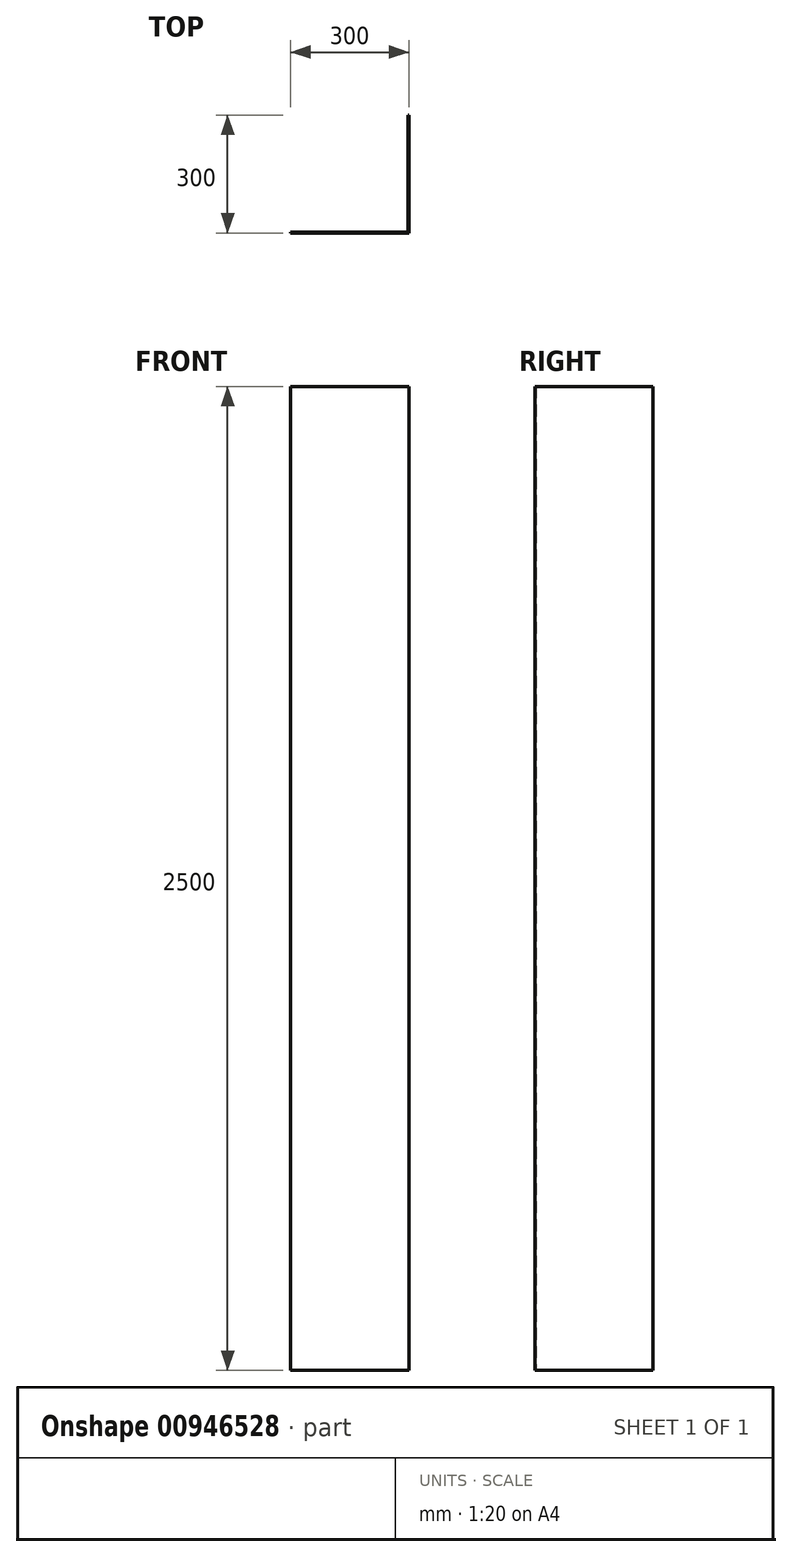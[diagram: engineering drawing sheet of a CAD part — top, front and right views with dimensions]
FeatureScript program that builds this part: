
annotation { "Feature Type Name" : "Feature", "Feature Type Description" : "" }
export const myFeature = defineFeature(function(context is Context, id is Id, definition is map)
    precondition{}
    {
        {
            var Q0;
            Q0=qCreatedBy(makeId("Top.planeOp"),FACE);
            var sketch = newSketch(context, id + "F0", { "sketchPlane" : qUnion([Q0])});
            skLineSegment(sketch, "E0", {"start": v(0, 0) * mm, "end": v(0, 300) * mm});
            skLineSegment(sketch, "E1", {"start": v(0, 300) * mm, "end": v(-2.5, 300) * mm});
            skLineSegment(sketch, "E2", {"start": v(-2.5, 300) * mm, "end": v(-2.5, 2.5) * mm});
            skLineSegment(sketch, "E3", {"start": v(-2.5, 2.5) * mm, "end": v(-300, 2.5) * mm});
            skLineSegment(sketch, "E4", {"start": v(-300, 2.5) * mm, "end": v(-300, 0) * mm});
            skLineSegment(sketch, "E5", {"start": v(-300, 0) * mm, "end": v(0, 0) * mm});
            skSolve(sketch);
        }
        {
            var Q0;
            Q0 = qSketchRegion(id + "F0", true);
            extrude(context, id + "F1", {"entities" : qUnion([Q0]), "depth" : 2500 * mm, "offsetDistance" : 25 * mm});
        }
    });
